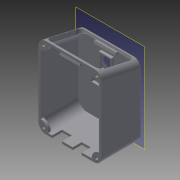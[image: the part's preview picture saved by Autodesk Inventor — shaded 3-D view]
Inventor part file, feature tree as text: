
AUTODESK INVENTOR PART (.ipt)
format: ipt  version: 2014 (Build 180170000, 170)  size: 415,232 bytes
history: native  units: mm
features: sketch x14, extrude x10, fillet x5, loft x2, chamfer x2, plane x1, projected_geometry x1
ambient origin geometry x8: Origin, YZ Plane, XZ Plane, XY Plane, X Axis, Y Axis, Z Axis, Center Point
bodies: Solid1 (feature_tree)
feature tree (35):
  sketch  "Sketch1"  dims[d0=70.0mm d1=90.0mm]
  plane  "Work Plane1"
  loft  "Loft1"
  sketch  "Sketch3"  dims[d6=0.0mm d7=90.0deg d8=60.0mm]
  sketch  "Sketch4"  dims[d9=40.0mm d10=65.0mm d11=85.0mm d12=65.0mm]
  sketch  "Sketch5"  dims[d13=75.0mm d14=5.0mm d15=0.0mm d16=5.0mm]
  extrude  "Extrusion1"  Depth=45.0mm
  fillet  "Fillet1"  [1 undecoded]
  loft  "Loft2"
  extrude  "Extrusion2"  Depth=65.0mm
  fillet  "Fillet2"  Radius=85.0mm
  fillet  "Fillet3"  Radius=65.0mm
  extrude  "Extrusion3"  Depth=5.0mm TaperAngle=0.0deg
  fillet  "Fillet4"  Radius=5.0mm
  extrude  "Extrusion4"  TaperAngle=0.0deg  [1 undecoded]
  extrude  "Extrusion5"  Depth=8.0mm
  extrude  "Extrusion6"  Depth=3.0mm TaperAngle=0.0deg
  chamfer  "Chamfer1"  Distance=3.0mm
  fillet  "Fillet5"  Radius=11.0mm
  extrude  "Extrusion7"  Depth=11.0mm
  extrude  "Extrusion8"  Depth=15.0mm
  chamfer  "Chamfer2"  Distance=3.0mm
  extrude  "Extrusion9"  Depth=10.0mm
  extrude  "Extrusion10"  Depth=3.0mm TaperAngle=0.0deg
  sketch  "Sketch2"  dims[d2=45.0mm d3=80.0mm d4=0.0mm d5=90.0deg]
  sketch  "Sketch6"  dims[d17=0.0mm d18=90.0deg d19=0.0mm d20=90.0deg]
  sketch  "Sketch7"  dims[d21=3.0mm d22=0.0mm d23=8.0mm]
  projected_geometry  "Projected Loop1"
  sketch  "Sketch8"  dims[d24=10.0mm d25=3.0mm d26=0.0mm]
  sketch  "Sketch9"  dims[d27=2.0mm]
  sketch  "Sketch10"  dims[d28=6.0mm d29=3.0mm d30=0.0mm d31=11.0mm]
  sketch  "Sketch11"  dims[d32=6.0mm d33=11.0mm]
  sketch  "Sketch12"  dims[d34=6.0mm d35=15.0mm]
  sketch  "Sketch13"  dims[d36=15.0mm]
  sketch  "Sketch14"  dims[d37=37.280029mm d38=3.0mm d39=0.0mm d40=10.0mm d41=3.0mm d42=0.0mm d43=15.0mm d44=3.0mm d45=2.0mm d46=45.0deg d47=3.0mm d48=18.0mm d49=18.0mm d50=18.0mm d51=18.0mm d52=3.0mm d53=0.0mm d54=2.5mm d55=2.5mm d56=2.5mm d57=2.5mm d58=3.0mm d59=0.0mm d60=0.5mm d61=2.0mm d62=45.0deg d63=11.0mm d64=11.0mm d65=10.0mm d66=10.0mm d67=3.0mm d68=0.0mm d69=11.0mm d70=13.0mm d71=2.0mm d72=1.5mm d73=1.5mm d74=1.5mm d75=1.5mm d76=3.0mm d77=0.0mm]
note: 2 required parameter values undecoded (feature->parameter linkage not recoverable at this tier; creation-order binding heuristic only, values carry confidence <= 0.55)
